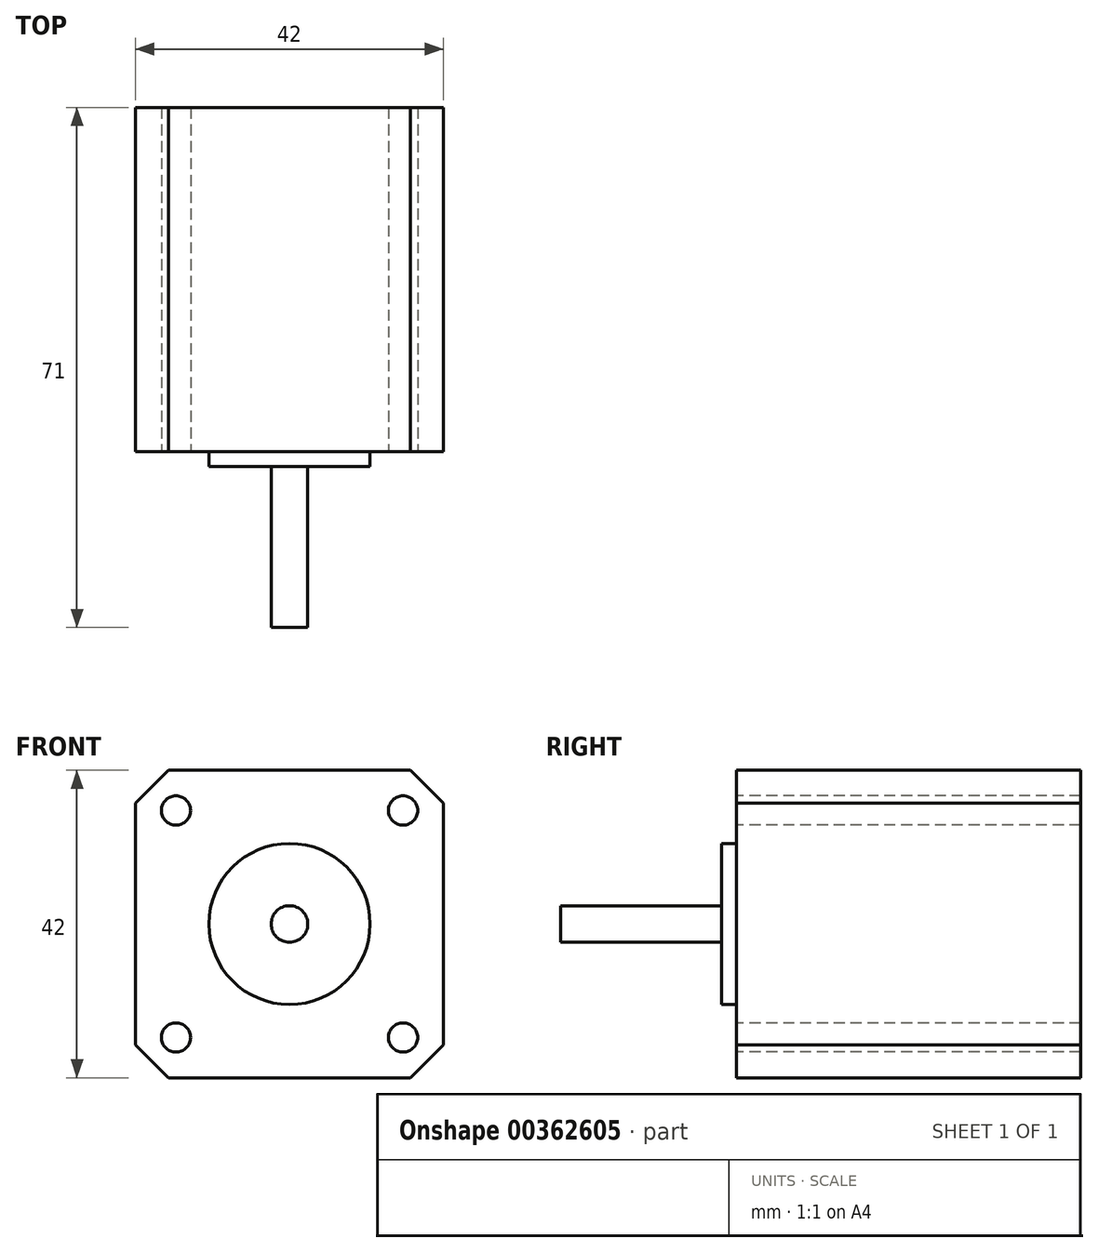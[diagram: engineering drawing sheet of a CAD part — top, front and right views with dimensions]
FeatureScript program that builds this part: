
annotation { "Feature Type Name" : "Feature", "Feature Type Description" : "" }
export const myFeature = defineFeature(function(context is Context, id is Id, definition is map)
    precondition{}
    {
        {
            var Q0;
            Q0=qCreatedBy(makeId("Front.planeOp"),FACE);
            var sketch = newSketch(context, id + "F0", { "sketchPlane" : qUnion([Q0])});
            skCircle(sketch, "E0", {"center": v(0, 0) * mm, "radius": 2.5 * mm});
            skSolve(sketch);
        }
        {
            var Q0;
            Q0=qCreatedBy(makeId("Front.planeOp"),FACE);
            var sketch = newSketch(context, id + "F1", { "sketchPlane" : qUnion([Q0])});
            skCircle(sketch, "E1", {"center": v(0, 0) * mm, "radius": 11 * mm});
            skSolve(sketch);
        }
        {
            var Q0;
            Q0=qCreatedBy(makeId("Front.planeOp"),FACE);
            var sketch = newSketch(context, id + "F2", { "sketchPlane" : qUnion([Q0])});
            skLineSegment(sketch, "E2.bottom", {"start": v(16.5, 21) * mm, "end": v(-16.5, 21) * mm});
            skLineSegment(sketch, "E2.top", {"start": v(16.5, -21) * mm, "end": v(-16.5, -21) * mm});
            skLineSegment(sketch, "E2.left", {"start": v(21, 16.5) * mm, "end": v(21, -16.5) * mm});
            skLineSegment(sketch, "E2.right", {"start": v(-21, 16.5) * mm, "end": v(-21, -16.5) * mm});
            skPoint(sketch, "E2.middle", {"position": v(0, 0) * mm});
            skPoint(sketch, "E3", {"position": v(-15.5, 15.5) * mm});
            skPoint(sketch, "E4", {"position": v(-15.5, -15.5) * mm});
            skPoint(sketch, "E5", {"position": v(15.5, 15.5) * mm});
            skPoint(sketch, "E6", {"position": v(15.5, -15.5) * mm});
            skLineSegment(sketch, "E7", {"start": v(-21, 16.5) * mm, "end": v(-16.5, 21) * mm});
            skLineSegment(sketch, "E8.MirrorCS", {"start": v(21, 16.5) * mm, "end": v(16.5, 21) * mm});
            skLineSegment(sketch, "E9.MirrorCS", {"start": v(-21, -16.5) * mm, "end": v(-16.5, -21) * mm});
            skLineSegment(sketch, "E10.MirrorCS", {"start": v(21, -16.5) * mm, "end": v(16.5, -21) * mm});
            skPoint(sketch, "E11.orphan", {"position": v(-21, 21) * mm});
            skPoint(sketch, "E12.orphan", {"position": v(21, 21) * mm});
            skPoint(sketch, "E13.orphan", {"position": v(21, -21) * mm});
            skPoint(sketch, "E14.orphan", {"position": v(-21, -21) * mm});
            skSolve(sketch);
        }
        {
            var Q0;
            Q0 = qSketchRegion(id + "F0", true);
            extrude(context, id + "F3", {"entities" : qUnion([Q0]), "depth" : 24 * mm});
        }
        {
            var Q0;
            Q0 = qSketchRegion(id + "F1", true);
            extrude(context, id + "F4", {"entities" : qUnion([Q0]), "operationType" : NewBodyOperationType.ADD, "depth" : 2 * mm});
        }
        {
            var Q0;
            Q0 = qSketchRegion(id + "F2", true);
            extrude(context, id + "F5", {"entities" : qUnion([Q0]), "operationType" : NewBodyOperationType.ADD, "oppositeDirection" : true, "depth" : 47 * mm});
        }
        {
            var Q0;
            Q0=qCreatedBy(makeId("Front.planeOp"),FACE);
            var sketch = newSketch(context, id + "F6", { "sketchPlane" : qUnion([Q0])});
            skPoint(sketch, "E15", {"position": v(-15.5, 15.5) * mm});
            skPoint(sketch, "E16", {"position": v(-15.5, -15.5) * mm});
            skPoint(sketch, "E17", {"position": v(15.5, 15.5) * mm});
            skPoint(sketch, "E18", {"position": v(15.5, -15.5) * mm});
            skSolve(sketch);
        }
        {
            var Q0;
            Q0=sQuery(id+"F6.wireOp",VERTEX,"E15");
            var Q1;
            Q1=sQuery(id+"F6.wireOp",VERTEX,"E17");
            var Q2;
            Q2=sQuery(id+"F6.wireOp",VERTEX,"E18");
            var Q3;
            Q3=sQuery(id+"F6.wireOp",VERTEX,"E16");
            var Q4;
            Q4=makeQuery(id+"F3.opExtrude","SWEPT_BODY",BODY,{"disambiguationData":[OSD([sQuery(id+"F0.wireOp",EDGE,"E0")])]});
            hole(context, id + "F7", {"style" : HoleStyle.SIMPLE, "endStyle" : HoleEndStyle.THROUGH, "holeDiameter" : 4 * mm, "isTappedThrough" : true, "tappedDepth" : 12 * mm, "tapClearance" : 3, "locations" : qUnion([Q0, Q1, Q2, Q3]), "scope" : qUnion([Q4])});
        }
    });
